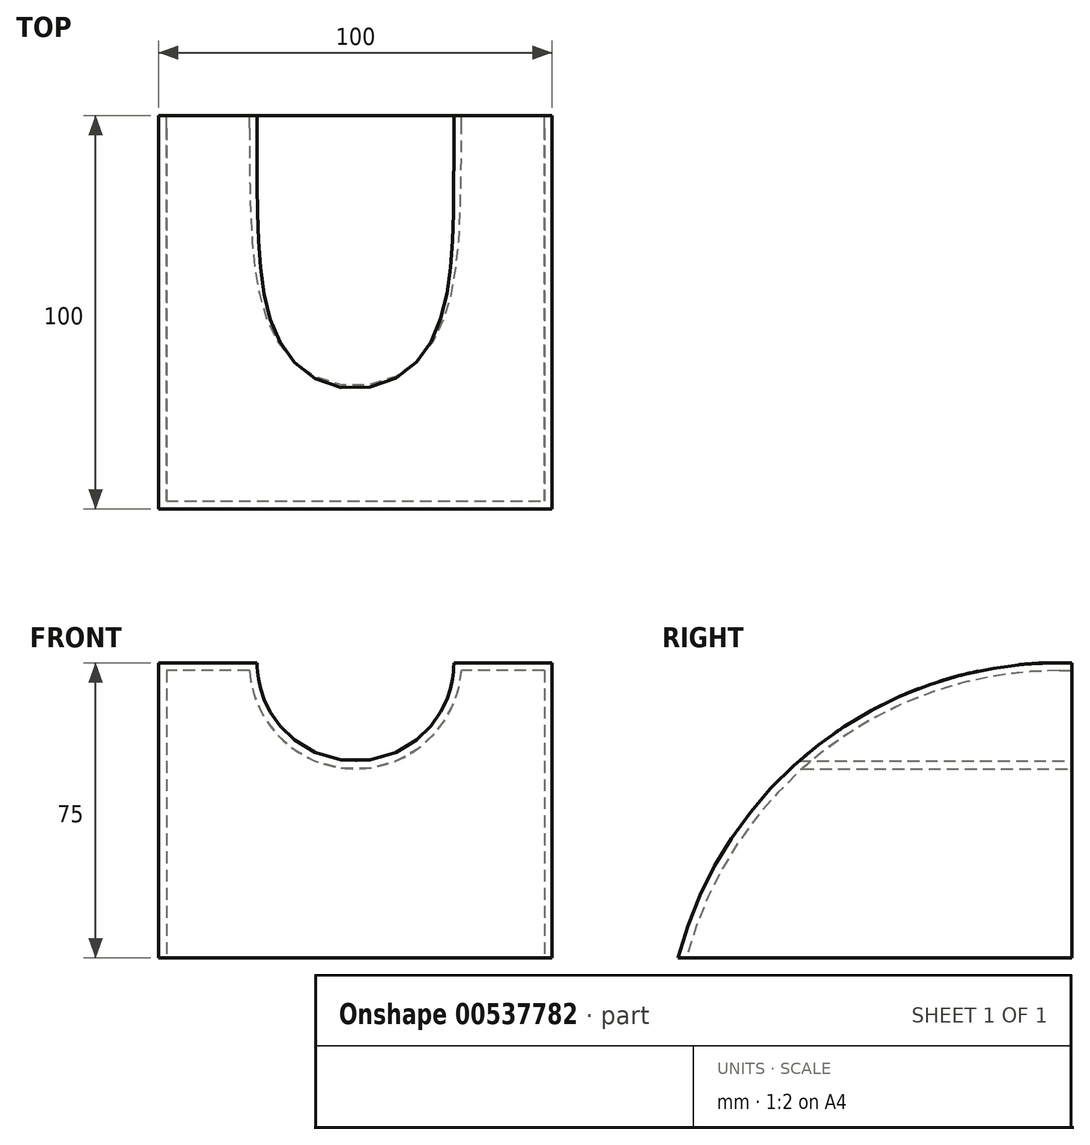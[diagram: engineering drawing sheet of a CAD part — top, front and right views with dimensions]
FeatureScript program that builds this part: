
annotation { "Feature Type Name" : "Feature", "Feature Type Description" : "" }
export const myFeature = defineFeature(function(context is Context, id is Id, definition is map)
    precondition{}
    {
        {
            var Q0;
            Q0=qCreatedBy(makeId("Front.planeOp"),FACE);
            var sketch = newSketch(context, id + "F0", { "sketchPlane" : qUnion([Q0])});
            skLineSegment(sketch, "E0.bottom", {"start": v(50, 37.5) * mm, "end": v(25, 37.5) * mm});
            skLineSegment(sketch, "E0.top", {"start": v(50, -37.5) * mm, "end": v(-50, -37.5) * mm});
            skLineSegment(sketch, "E0.left", {"start": v(50, 37.5) * mm, "end": v(50, -37.5) * mm});
            skLineSegment(sketch, "E0.right", {"start": v(-50, 37.5) * mm, "end": v(-50, -37.5) * mm});
            skPoint(sketch, "E0.middle", {"position": v(0, 0) * mm});
            skArc(sketch, "E1", {"start": v(-25, 37.5) * mm, "mid": v(0, 12.5) * mm, "end": v(25, 37.5) * mm});
            skLineSegment(sketch, "E2.trimOffspring", {"start": v(-25, 37.5) * mm, "end": v(-50, 37.5) * mm});
            skSolve(sketch);
        }
        {
            var Q0;
            Q0=makeQuery(id+"F0.imprint","IMPRINT",FACE,{"disambiguationData":[TD([[makeQuery(id+"F0.imprint","IMPRINT",EDGE,{"derivedFrom":sQuery(id+"F0.wireOp",EDGE,"E0.bottom")}),1.0]])]});
            extrude(context, id + "F1", {"entities" : qUnion([Q0]), "endBound" : BoundingType.SYMMETRIC, "depth" : 100 * mm, "offsetDistance" : 25 * mm});
        }
        {
            var Q0;
            Q0=makeQuery(id+"F1.opExtrude","CAP_EDGE",EDGE,{"disambiguationData":[OSD([sQuery(id+"F0.wireOp",EDGE,"E0.bottom")])],"isStart":false});
            fillet(context, id + "F2", {"entities" : qUnion([Q0]), "radius" : 100 * mm, "tangentPropagation" : true, "allowEdgeOverflow" : false});
        }
        {
            var Q0;
            Q0=makeQuery(id+"F1.opExtrude","CAP_FACE",FACE,{"disambiguationData":[OSD([sQuery(id+"F0.wireOp",EDGE,"E0.bottom"),sQuery(id+"F0.wireOp",EDGE,"E0.top"),sQuery(id+"F0.wireOp",EDGE,"E0.left"),sQuery(id+"F0.wireOp",EDGE,"E0.right")])],"isStart":true});
            var Q1;
            Q1=makeQuery(id+"F1.opExtrude","SWEPT_FACE",FACE,{"disambiguationData":[OSD([sQuery(id+"F0.wireOp",EDGE,"E0.top")])]});
            shell(context, id + "F3", {"entities" : qUnion([Q0, Q1]), "thickness" : 2 * mm});
        }
    });
